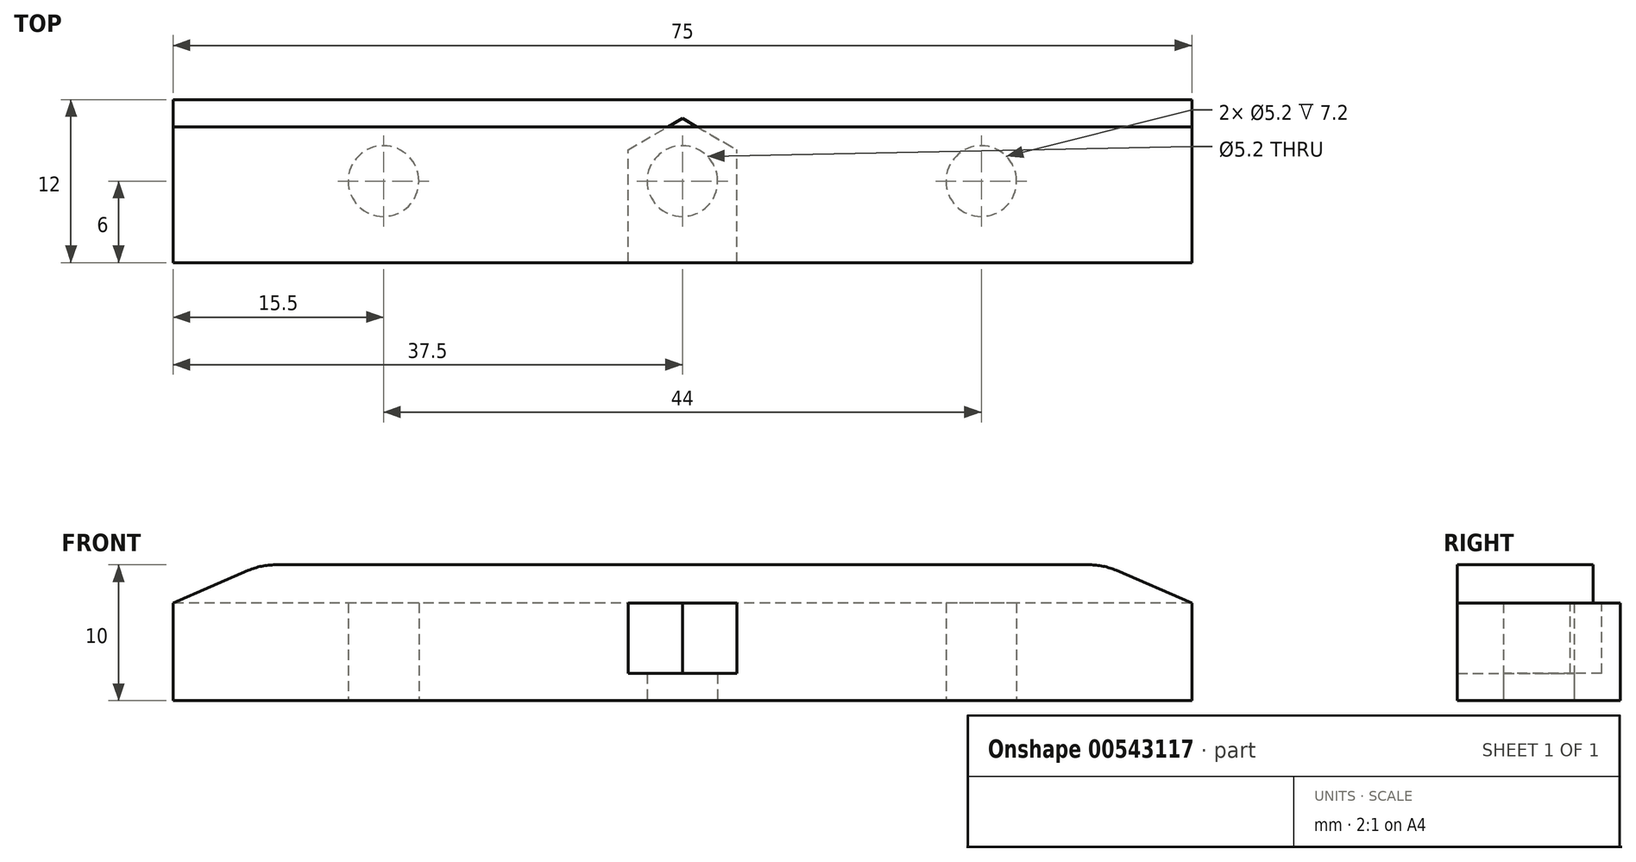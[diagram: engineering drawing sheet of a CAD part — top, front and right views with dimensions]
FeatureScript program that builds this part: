
annotation { "Feature Type Name" : "Feature", "Feature Type Description" : "" }
export const myFeature = defineFeature(function(context is Context, id is Id, definition is map)
    precondition{}
    {
        {
            var Q0;
            Q0=qCreatedBy(makeId("Top.planeOp"),FACE);
            var sketch = newSketch(context, id + "F0", { "sketchPlane" : qUnion([Q0])});
            skLineSegment(sketch, "E0.bottom", {"start": v(37.5, 6) * mm, "end": v(-37.5, 6) * mm});
            skLineSegment(sketch, "E0.top", {"start": v(37.5, -6) * mm, "end": v(-37.5, -6) * mm});
            skLineSegment(sketch, "E0.left", {"start": v(37.5, 6) * mm, "end": v(37.5, -6) * mm});
            skLineSegment(sketch, "E0.right", {"start": v(-37.5, 6) * mm, "end": v(-37.5, -6) * mm});
            skPoint(sketch, "E0.middle", {"position": v(0, 0) * mm});
            skCircle(sketch, "E1", {"center": v(0, 0) * mm, "radius": 2.6 * mm});
            skCircle(sketch, "E2", {"center": v(22, 0) * mm, "radius": 2.6 * mm});
            skCircle(sketch, "E3", {"center": v(-22, 0) * mm, "radius": 2.6 * mm});
            skSolve(sketch);
        }
        {
            var Q0;
            Q0=makeQuery(id+"F0.imprint","IMPRINT",FACE,{"disambiguationData":[TD([[makeQuery(id+"F0.imprint","IMPRINT",EDGE,{"derivedFrom":sQuery(id+"F0.wireOp",EDGE,"E0.bottom")}),1.0]])]});
            extrude(context, id + "F1", {"entities" : qUnion([Q0]), "depth" : 7.2 * mm, "offsetDistance" : 25 * mm});
        }
        {
            var Q0;
            Q0=makeQuery(id+"F1.opExtrude","CAP_FACE",FACE,{"disambiguationData":[OSD([sQuery(id+"F0.wireOp",EDGE,"E0.bottom"),sQuery(id+"F0.wireOp",EDGE,"E0.top"),sQuery(id+"F0.wireOp",EDGE,"E0.left"),sQuery(id+"F0.wireOp",EDGE,"E0.right"),sQuery(id+"F0.wireOp",EDGE,"E1"),sQuery(id+"F0.wireOp",EDGE,"E2"),sQuery(id+"F0.wireOp",EDGE,"E3")])],"isStart":false});
            var sketch = newSketch(context, id + "F2", { "sketchPlane" : qUnion([Q0])});
            skCircle(sketch, "E4.cCircle", {"center": v(0, 0) * mm, "radius": 4 * mm, "construction": true});
            skLineSegment(sketch, "E4.0", {"start": v(4, 2.3) * mm, "end": v(4, -2.3) * mm});
            skLineSegment(sketch, "E4.3", {"start": v(-4, -2.3) * mm, "end": v(-4, 2.3) * mm});
            skLineSegment(sketch, "E4.4", {"start": v(-4, 2.3) * mm, "end": v(0, 4.62) * mm});
            skLineSegment(sketch, "E4.5", {"start": v(0, 4.62) * mm, "end": v(4, 2.3) * mm});
            skPoint(sketch, "E4.0.midPoint", {"position": v(4, 0) * mm});
            skLineSegment(sketch, "E5", {"start": v(-4, -2.3) * mm, "end": v(-4, -6) * mm});
            skLineSegment(sketch, "E6", {"start": v(-4, -6) * mm, "end": v(4, -6) * mm});
            skLineSegment(sketch, "E7", {"start": v(4, -6) * mm, "end": v(4, -2.3) * mm});
            skSolve(sketch);
        }
        {
            var Q0;
            Q0=makeQuery(id+"F2.imprint","IMPRINT",FACE,{"disambiguationData":[TD([[makeQuery(id+"F2.imprint","IMPRINT",EDGE,{"derivedFrom":sQuery(id+"F2.wireOp",EDGE,"E4.0")}),-1.0]])]});
            extrude(context, id + "F3", {"entities" : qUnion([Q0]), "operationType" : NewBodyOperationType.REMOVE, "oppositeDirection" : true, "depth" : 5.2 * mm, "offsetDistance" : 25 * mm});
        }
        {
            var Q0;
            Q0=makeQuery(id+"F1.opExtrude","SWEPT_FACE",FACE,{"disambiguationData":[OSD([sQuery(id+"F0.wireOp",EDGE,"E0.top")])]});
            var sketch = newSketch(context, id + "F4", { "sketchPlane" : qUnion([Q0])});
            skLineSegment(sketch, "E8", {"start": v(0, 0) * mm, "end": v(0, 10) * mm, "construction": true});
            skLineSegment(sketch, "E9", {"start": v(-31, 10) * mm, "end": v(31, 10) * mm});
            skPoint(sketch, "E10", {"position": v(0, 10) * mm});
            skLineSegment(sketch, "E11", {"start": v(-31, 10) * mm, "end": v(-37.5, 7.2) * mm});
            skLineSegment(sketch, "E12", {"start": v(-37.5, 7.2) * mm, "end": v(37.5, 7.2) * mm});
            skLineSegment(sketch, "E13", {"start": v(37.5, 7.2) * mm, "end": v(31, 10) * mm});
            skSolve(sketch);
        }
        {
            var Q0;
            Q0=makeQuery(id+"F4.imprint","IMPRINT",FACE,{"disambiguationData":[TD([[makeQuery(id+"F4.imprint","IMPRINT",EDGE,{"derivedFrom":sQuery(id+"F4.wireOp",EDGE,"E9")}),-1.0]])]});
            extrude(context, id + "F5", {"entities" : qUnion([Q0]), "operationType" : NewBodyOperationType.ADD, "oppositeDirection" : true, "depth" : 10 * mm, "offsetDistance" : 25 * mm});
        }
        {
            var Q0;
            Q0=makeQuery(id+"F5.opExtrude","SWEPT_EDGE",EDGE,{"disambiguationData":[OSD([sQuery(id+"F4.wireOp",EDGE,"E9"),sQuery(id+"F4.wireOp",EDGE,"E11")])]});
            var Q1;
            Q1=makeQuery(id+"F5.opExtrude","SWEPT_EDGE",EDGE,{"disambiguationData":[OSD([sQuery(id+"F4.wireOp",EDGE,"E9"),sQuery(id+"F4.wireOp",EDGE,"E13")])]});
            fillet(context, id + "F6", {"entities" : qUnion([Q0, Q1]), "radius" : 5 * mm, "tangentPropagation" : true, "allowEdgeOverflow" : false});
        }
    });
